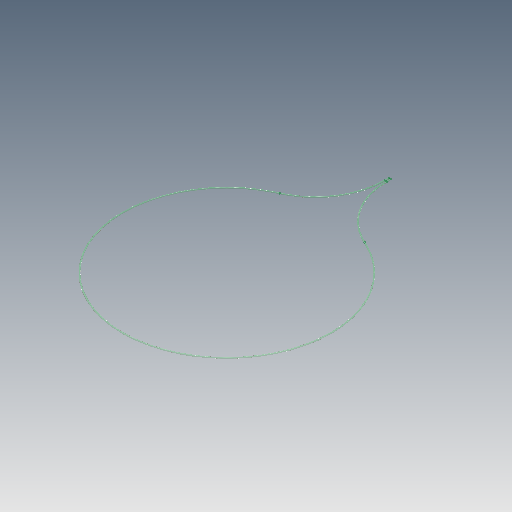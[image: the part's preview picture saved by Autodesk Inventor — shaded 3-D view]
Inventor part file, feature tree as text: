
AUTODESK INVENTOR PART (.ipt)
format: ipt  version: 2020 (Build 240168000, 168)  size: 167,424 bytes
history: native  units: mm
features: extrude x2, sketch x2, projected_geometry x2, fillet x1
ambient origin geometry x8: Origin, YZ Plane, XZ Plane, XY Plane, X Axis, Y Axis, Z Axis, Center Point
bodies: Solid1 (feature_tree)
feature tree (7):
  extrude  "Extrusion1"  Depth=0.98mm
  fillet  "Fillet1"  Radius=0.16mm
  extrude  "Extrusion2"  Depth=0.49mm
  sketch  "Sketch1"  dims[d16=0.16mm d17=0.98mm d18=0.16mm]
  sketch  "Sketch2"  dims[d19=150.0mm d20=0.16mm d21=0.98mm d22=0.16mm d23=100.0mm d24=0.05mm d25=1.0mm d26=100.0mm d27=10.0mm d28=0.16mm d29=0.98mm d30=0.16mm d31=100.0mm d32=0.05mm d33=1.0mm d34=100.0mm d35=10.0mm d36=0.98mm d37=0.0mm d38=0.49mm d39=3.0mm d40=0.0mm d41=0.5mm d42=0.872665mm d43=0.5mm d44=0.872665mm]
  projected_geometry  "Projected Loop1"
  projected_geometry  "Projected Loop2"
